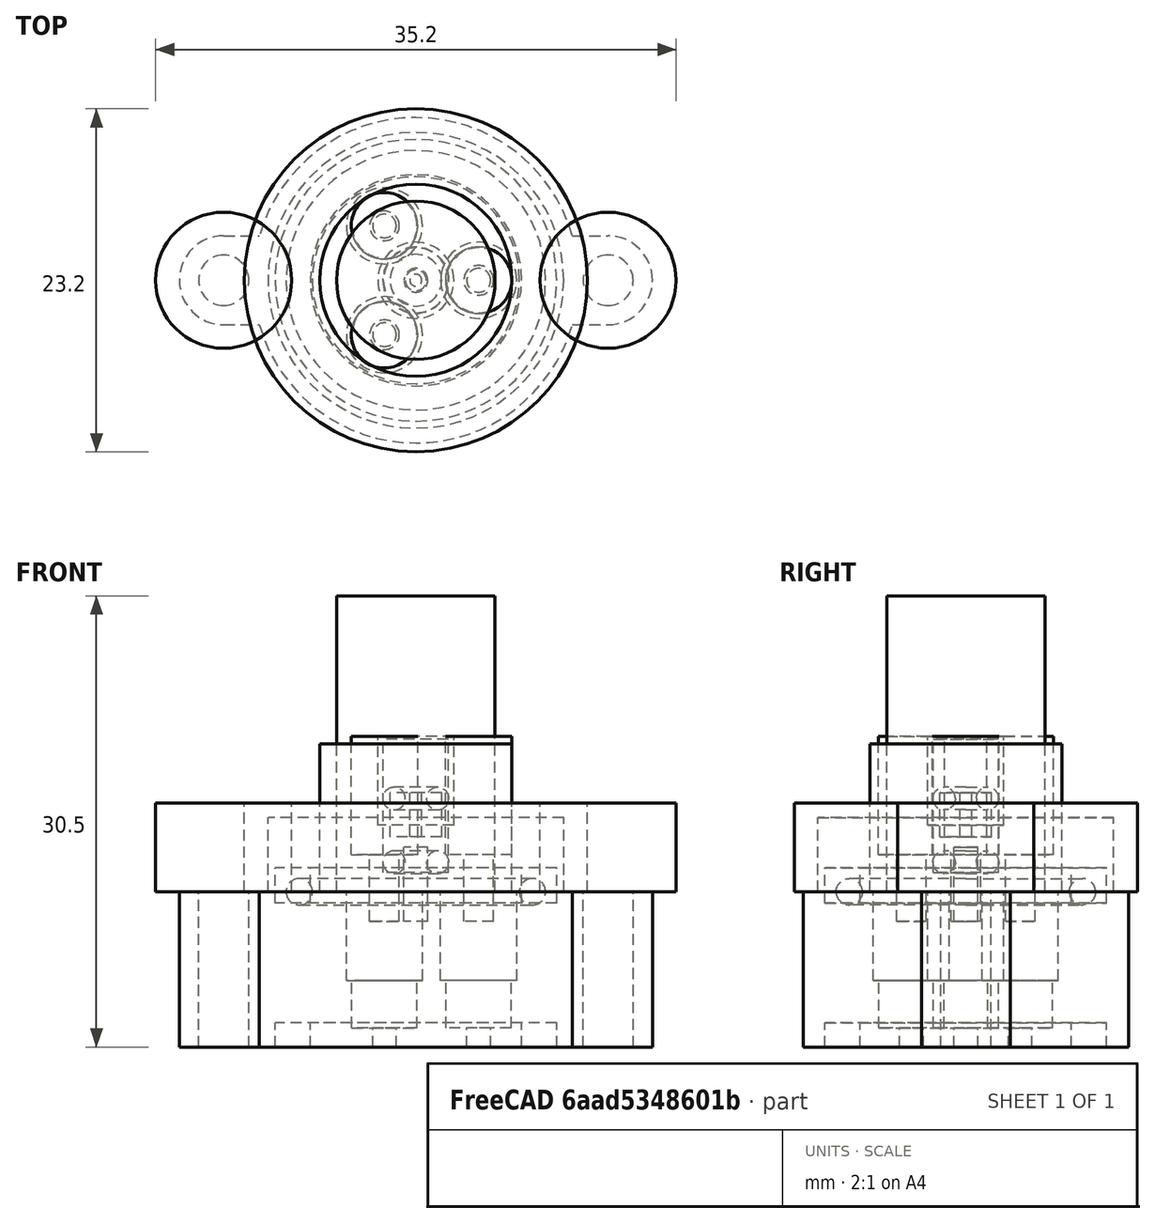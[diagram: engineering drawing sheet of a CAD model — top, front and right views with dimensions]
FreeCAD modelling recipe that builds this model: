
FCSTD DOCUMENT  (FreeCAD 0.17R13509 (Git))
Label: aluminium_ft_insert
License: All rights reserved
LicenseURL: http://en.wikipedia.org/wiki/All_rights_reserved
objects: Part::Cylinder×46, Part::MultiFuse×10, Part::Cut×8, Part::Box×6, Part::FeaturePython×4, Part::Feature×3, App::FeaturePython×1
note: 77 computed .brp shape members not serialized (recipe doc carries the construction recipe); baked Part::Feature solids carry a one-line shape summary decoded from their .brp

FEATURE [Part::Cylinder] Cylinder155  label="Cylinder009"
  Angle = 360
  AttacherType = Attacher::AttachEngine3D
  Height = 2.38125
  Radius = 9.525
  expr: Radius = 3 / 4 * 25.399999999999999 / 2
  expr: Height = 3 / 32 * 25.399999999999999
FEATURE [Part::Cylinder] Cylinder154  label="Cylinder008"
  Angle = 360
  AttacherType = Attacher::AttachEngine3D
  Height = 2.38125
  Radius = 7.14375
  expr: Radius = 9 / 16 * 25.399999999999999 / 2
  expr: Height = 3 / 32 * 25.399999999999999
FEATURE [Part::Feature] Part__Feature001  label="TopOring"
  Placement = pos=(0,0,6.3) rot=(0,0,1;0rad)
  shape: bbox 4.839 x 4.839 x 1.524 mm, 4 faces (baked)
FEATURE [Part::Feature] Part__Feature002  label="BottomOring"
  Placement = pos=(0,0,2) rot=(0,0,1;0rad)
  shape: bbox 4.839 x 4.839 x 1.524 mm, 4 faces (baked)
FEATURE [Part::Cylinder] Cylinder153  label="Body"
  Angle = 360
  AttacherType = Attacher::AttachEngine3D
  Height = 5
  Radius = 10
FEATURE [Part::Cut] Cut019  label="Oring"
  Base = -> Cylinder155
  Placement = pos=(0,0,-0.75) rot=(0,0,1;0rad)
  Tool = -> Cylinder154
FEATURE [Part::Cylinder] Cylinder147  label="ThreadedSection"
  Angle = 360
  AttacherType = Attacher::AttachEngine3D
  Height = 1
  Placement = pos=(0,0,4.5) rot=(0,0,1;0rad)
  Radius = 1
FEATURE [Part::Cylinder] Cylinder149  label="FTBead"
  Angle = 360
  AttacherType = Attacher::AttachEngine3D
  Height = 3
  Placement = pos=(0,0,2.7) rot=(0,0,1;0rad)
  Radius = 1.75
  expr: Radius = 3.5 / 2
FEATURE [Part::Cylinder] Cylinder152  label="RFFeeds005"
  Angle = 360
  AttacherType = Attacher::AttachEngine3D
  Height = 20
  Radius = 5.35813
  expr: Placement.Base.x = 0
FEATURE [Part::Cylinder] Cylinder156  label="BottomWireOutlet"
  Angle = 360
  AttacherType = Attacher::AttachEngine3D
  Height = 5
  Placement = pos=(0,0,-2) rot=(0,0,1;0rad)
  Radius = 1
FEATURE [Part::Cylinder] Cylinder157  label="SealSubtraction"
  Angle = 360
  AttacherType = Attacher::AttachEngine3D
  Height = 8
  Placement = pos=(0,0,2.5) rot=(0,0,1;0rad)
  Radius = 2.25
FEATURE [Part::MultiFuse] Fusion
  Placement = pos=(4.25,0,0) rot=(0,0,1;0rad)
  Shapes = -> [Cylinder147,Cylinder157,Cylinder156]
FEATURE [Part::FeaturePython] Array  label="SealArray"  # Draft array (typed FeaturePython)
  Angle = 360
  ArrayType = 1
  Axis = (0,0,1)
  Base = -> Fusion
  Center = (0,0,0)
  Fuse = false
  IntervalAxis = (0,0,0)
  IntervalX = (1,0,0)
  IntervalY = (0,1,0)
  IntervalZ = (0,0,0)
  NumberPolar = 3
  NumberX = 2
  NumberY = 2
  NumberZ = 1
FEATURE [Part::Cylinder] Cylinder159  label="FTBeadHole"
  Angle = 360
  AttacherType = Attacher::AttachEngine3D
  Height = 17
  Radius = 0.405
  expr: Radius = 0.81000000000000005 / 2
FEATURE [Part::Cut] Cut020
  Base = -> Cylinder149
  Placement = pos=(0,0,1) rot=(0,0,1;0rad)
  Tool = -> Cylinder159
FEATURE [Part::Cylinder] Cylinder160  label="Cylinder010"
  Angle = 360
  AttacherType = Attacher::AttachEngine3D
  Height = 2.38125
  Radius = 9.525
  expr: Radius = 3 / 4 * 25.399999999999999 / 2
  expr: Height = 3 / 32 * 25.399999999999999
FEATURE [Part::Cylinder] Cylinder161  label="WireFeedsMount003"
  Angle = 360
  AttacherType = Attacher::AttachEngine3D
  Height = 11
  Placement = pos=(-13,0,0) rot=(0,0,1;0rad)
  Radius = 1.7
FEATURE [Part::Cylinder] Cylinder162  label="ThreadedSection001"
  Angle = 360
  AttacherType = Attacher::AttachEngine3D
  Height = 6
  Placement = pos=(0,0,4.5) rot=(0,0,1;0rad)
  Radius = 2.575
  expr: Radius = 5.1500000000000004 / 2
FEATURE [Part::Cylinder] Cylinder163  label="Cylinder011"
  Angle = 360
  AttacherType = Attacher::AttachEngine3D
  Height = 2.38125
  Radius = 7.14375
  expr: Radius = 9 / 16 * 25.399999999999999 / 2
  expr: Height = 3 / 32 * 25.399999999999999
FEATURE [Part::Cut] Cut022  label="Oring001"
  Base = -> Cylinder160
  Placement = pos=(0,0,-0.75) rot=(0,0,1;0rad)
  Tool = -> Cylinder163
FEATURE [Part::Cylinder] Cylinder164  label="Body001"
  Angle = 360
  AttacherType = Attacher::AttachEngine3D
  Height = 10.5
  Radius = 11
FEATURE [Part::Cylinder] Cylinder165  label="WireFeedsMount004"
  Angle = 360
  AttacherType = Attacher::AttachEngine3D
  Height = 11
  Placement = pos=(13,0,0) rot=(0,0,1;0rad)
  Radius = 1.7
FEATURE [Part::Cylinder] Cylinder166  label="BottomWireOutlet001"
  Angle = 360
  AttacherType = Attacher::AttachEngine3D
  Height = 5
  Placement = pos=(0,0,-2) rot=(0,0,1;0rad)
  Radius = 0.8
FEATURE [Part::Cylinder] Cylinder167  label="SealSubtraction001"
  Angle = 360
  AttacherType = Attacher::AttachEngine3D
  Height = 9
  Placement = pos=(0,0,1.3) rot=(0,0,1;0rad)
  Radius = 2.2
FEATURE [Part::Box] Box002  label="MountCube003"
  AttacherType = Attacher::AttachEngine3D
  Height = 10.5
  Length = 3
  Placement = pos=(10,-3,0) rot=(0,0,1;0rad)
  Width = 6
FEATURE [Part::Box] Box003  label="MountCube004"
  AttacherType = Attacher::AttachEngine3D
  Height = 10.5
  Length = 3
  Placement = pos=(-13,-3,0) rot=(0,0,1;0rad)
  Width = 6
FEATURE [Part::MultiFuse] Fusion004
  Placement = pos=(4.25,0,0) rot=(0,0,1;0rad)
  Shapes = -> [Cylinder162,Cylinder167,Cylinder166]
FEATURE [Part::Cylinder] Cylinder168  label="MountFlange003"
  Angle = 360
  AttacherType = Attacher::AttachEngine3D
  Height = 10.5
  Placement = pos=(-13,0,0) rot=(0,0,1;0rad)
  Radius = 3
FEATURE [Part::Cylinder] Cylinder169  label="MountFlange004"
  Angle = 360
  AttacherType = Attacher::AttachEngine3D
  Height = 10.5
  Placement = pos=(13,0,0) rot=(0,0,1;0rad)
  Radius = 3
FEATURE [Part::MultiFuse] Fusion003
  Shapes = -> [Cylinder169,Box002,Box003,Cylinder168,Cylinder164]
FEATURE [Part::FeaturePython] Array001  label="SealArray001"  # Draft array (typed FeaturePython)
  Angle = 360
  ArrayType = 1
  Axis = (0,0,1)
  Base = -> Fusion004
  Center = (0,0,0)
  Fuse = false
  IntervalAxis = (0,0,0)
  IntervalX = (1,0,0)
  IntervalY = (0,1,0)
  IntervalZ = (0,0,0)
  NumberPolar = 3
  NumberX = 2
  NumberY = 2
  NumberZ = 1
FEATURE [Part::MultiFuse] Fusion005
  Shapes = -> [Cylinder165,Cylinder161,Cut022,Array001]
FEATURE [Part::Cut] Cut021
  Base = -> Fusion003
  Placement = pos=(0,0,-10.5) rot=(0,0,1;0rad)
  Tool = -> Fusion005
FEATURE [Part::Cylinder] Cylinder170  label="Cylinder012"
  Angle = 360
  AttacherType = Attacher::AttachEngine3D
  Height = 2.38125
  Radius = 9.525
  expr: Radius = 3 / 4 * 25.399999999999999 / 2
  expr: Height = 3 / 32 * 25.399999999999999
FEATURE [Part::Cylinder] Cylinder171  label="WireFeedsMount005"
  Angle = 360
  AttacherType = Attacher::AttachEngine3D
  Height = 11
  Placement = pos=(-13,0,0) rot=(0,0,1;0rad)
  Radius = 1.7
FEATURE [Part::Cylinder] Cylinder172  label="ThreadedSection002"
  Angle = 360
  AttacherType = Attacher::AttachEngine3D
  Height = 6
  Placement = pos=(0,0,4.5) rot=(0,0,1;0rad)
  Radius = 2.575
  expr: Radius = 5.1500000000000004 / 2
FEATURE [Part::Cylinder] Cylinder173  label="Cylinder013"
  Angle = 360
  AttacherType = Attacher::AttachEngine3D
  Height = 2.38125
  Radius = 7.14375
  expr: Radius = 9 / 16 * 25.399999999999999 / 2
  expr: Height = 3 / 32 * 25.399999999999999
FEATURE [Part::Cut] Cut024  label="Oring002"
  Base = -> Cylinder170
  Placement = pos=(0,0,-0.75) rot=(0,0,1;0rad)
  Tool = -> Cylinder173
FEATURE [Part::Cylinder] Cylinder174  label="Body002"
  Angle = 360
  AttacherType = Attacher::AttachEngine3D
  Height = 10.5
  Radius = 11
FEATURE [Part::Cylinder] Cylinder175  label="WireFeedsMount006"
  Angle = 360
  AttacherType = Attacher::AttachEngine3D
  Height = 11
  Placement = pos=(13,0,0) rot=(0,0,1;0rad)
  Radius = 1.7
FEATURE [Part::Cylinder] Cylinder176  label="BottomWireOutlet002"
  Angle = 360
  AttacherType = Attacher::AttachEngine3D
  Height = 5
  Placement = pos=(0,0,-2) rot=(0,0,1;0rad)
  Radius = 0.8
FEATURE [Part::Cylinder] Cylinder177  label="SealSubtraction002"
  Angle = 360
  AttacherType = Attacher::AttachEngine3D
  Height = 9
  Placement = pos=(0,0,1.3) rot=(0,0,1;0rad)
  Radius = 2.2
FEATURE [Part::Box] Box004  label="MountCube005"
  AttacherType = Attacher::AttachEngine3D
  Height = 10.5
  Length = 3
  Placement = pos=(10,-3,0) rot=(0,0,1;0rad)
  Width = 6
FEATURE [App::FeaturePython] SetupSheet002  # Path/CAM operation (typed FeaturePython)
  ClearanceHeightExpression = StartDepth+SetupSheet.ClearanceHeightOffset
  ClearanceHeightOffset = 5
  FinalDepthExpression = OpFinalDepth
  HorizRapid = 0
  SafeHeightExpression = StartDepth+SetupSheet.SafeHeightOffset
  SafeHeightOffset = 3
  StartDepthExpression = OpStartDepth
  StepDownExpression = OpToolDiameter
  VertRapid = 0
FEATURE [Part::Box] Box005  label="MountCube006"
  AttacherType = Attacher::AttachEngine3D
  Height = 10.5
  Length = 3
  Placement = pos=(-13,-3,0) rot=(0,0,1;0rad)
  Width = 6
FEATURE [Part::MultiFuse] Fusion007
  Placement = pos=(4.25,0,0) rot=(0,0,1;0rad)
  Shapes = -> [Cylinder172,Cylinder177,Cylinder176]
FEATURE [Part::Cylinder] Cylinder178  label="MountFlange005"
  Angle = 360
  AttacherType = Attacher::AttachEngine3D
  Height = 10.5
  Placement = pos=(-13,0,0) rot=(0,0,1;0rad)
  Radius = 3
FEATURE [Part::Cylinder] Cylinder179  label="MountFlange006"
  Angle = 360
  AttacherType = Attacher::AttachEngine3D
  Height = 10.5
  Placement = pos=(13,0,0) rot=(0,0,1;0rad)
  Radius = 3
FEATURE [Part::MultiFuse] Fusion006
  Shapes = -> [Cylinder179,Box004,Box005,Cylinder178,Cylinder174]
FEATURE [Part::FeaturePython] Array002  label="SealArray002"  # Draft array (typed FeaturePython)
  Angle = 360
  ArrayType = 1
  Axis = (0,0,1)
  Base = -> Fusion007
  Center = (0,0,0)
  Fuse = false
  IntervalAxis = (0,0,0)
  IntervalX = (1,0,0)
  IntervalY = (0,1,0)
  IntervalZ = (0,0,0)
  NumberPolar = 3
  NumberX = 2
  NumberY = 2
  NumberZ = 1
FEATURE [Part::MultiFuse] Fusion008
  Shapes = -> [Cylinder175,Cylinder171,Cut024,Array002]
FEATURE [Part::Cut] Cut023
  Base = -> Fusion006
  Placement = pos=(0,0,-10.5) rot=(0,0,1;0rad)
  Tool = -> Fusion008
FEATURE [Part::Cylinder] Cylinder180  label="Cylinder014"
  Angle = 360
  AttacherType = Attacher::AttachEngine3D
  Height = 2.38125
  Radius = 7.14375
  expr: Radius = 9 / 16 * 25.399999999999999 / 2
  expr: Height = 3 / 32 * 25.399999999999999
FEATURE [Part::Cylinder] Cylinder181  label="MountFlange007"
  Angle = 360
  AttacherType = Attacher::AttachEngine3D
  Height = 10.5
  Placement = pos=(-13,0,0) rot=(0,0,1;0rad)
  Radius = 3
FEATURE [Part::Box] Box006  label="MountCube007"
  AttacherType = Attacher::AttachEngine3D
  Height = 10.5
  Length = 3
  Placement = pos=(-13,-3,0) rot=(0,0,1;0rad)
  Width = 6
FEATURE [Part::Cylinder] Cylinder182  label="WireFeedsMount007"
  Angle = 360
  AttacherType = Attacher::AttachEngine3D
  Height = 11
  Placement = pos=(13,0,0) rot=(0,0,1;0rad)
  Radius = 1.7
FEATURE [Part::Box] Box007  label="MountCube008"
  AttacherType = Attacher::AttachEngine3D
  Height = 10.5
  Length = 3
  Placement = pos=(10,-3,0) rot=(0,0,1;0rad)
  Width = 6
FEATURE [Part::Cylinder] Cylinder183  label="WireFeedsMount008"
  Angle = 360
  AttacherType = Attacher::AttachEngine3D
  Height = 11
  Placement = pos=(-13,0,0) rot=(0,0,1;0rad)
  Radius = 1.7
FEATURE [Part::Cylinder] Cylinder184  label="Body003"
  Angle = 360
  AttacherType = Attacher::AttachEngine3D
  Height = 10.5
  Radius = 11
FEATURE [Part::Cylinder] Cylinder185  label="MountFlange008"
  Angle = 360
  AttacherType = Attacher::AttachEngine3D
  Height = 10.5
  Placement = pos=(13,0,0) rot=(0,0,1;0rad)
  Radius = 3
FEATURE [Part::Cylinder] Cylinder186  label="BottomWireOutlet003"
  Angle = 360
  AttacherType = Attacher::AttachEngine3D
  Height = 5
  Placement = pos=(0,0,-2) rot=(0,0,1;0rad)
  Radius = 0.8
FEATURE [Part::MultiFuse] Fusion011
  Shapes = -> [Cylinder185,Box007,Box006,Cylinder181,Cylinder184]
FEATURE [Part::Cylinder] Cylinder187  label="ThreadedSection003"
  Angle = 360
  AttacherType = Attacher::AttachEngine3D
  Height = 6
  Placement = pos=(0,0,4.5) rot=(0,0,1;0rad)
  Radius = 2.575
  expr: Radius = 5.1500000000000004 / 2
FEATURE [Part::Cylinder] Cylinder188  label="Cylinder015"
  Angle = 360
  AttacherType = Attacher::AttachEngine3D
  Height = 2.38125
  Radius = 9.525
  expr: Radius = 3 / 4 * 25.399999999999999 / 2
  expr: Height = 3 / 32 * 25.399999999999999
FEATURE [Part::Cut] Cut025  label="Oring003"
  Base = -> Cylinder188
  Placement = pos=(0,0,-0.75) rot=(0,0,1;0rad)
  Tool = -> Cylinder180
FEATURE [Part::Cylinder] Cylinder189  label="SealSubtraction003"
  Angle = 360
  AttacherType = Attacher::AttachEngine3D
  Height = 9
  Placement = pos=(0,0,1.3) rot=(0,0,1;0rad)
  Radius = 2.2
FEATURE [Part::MultiFuse] Fusion009
  Placement = pos=(4.25,0,0) rot=(0,0,1;0rad)
  Shapes = -> [Cylinder187,Cylinder189,Cylinder186]
FEATURE [Part::FeaturePython] Array003  label="SealArray003"  # Draft array (typed FeaturePython)
  Angle = 360
  ArrayType = 1
  Axis = (0,0,1)
  Base = -> Fusion009
  Center = (0,0,0)
  Fuse = false
  IntervalAxis = (0,0,0)
  IntervalX = (1,0,0)
  IntervalY = (0,1,0)
  IntervalZ = (0,0,0)
  NumberPolar = 3
  NumberX = 2
  NumberY = 2
  NumberZ = 1
FEATURE [Part::MultiFuse] Fusion010
  Shapes = -> [Cylinder182,Cylinder183,Cut025,Array003]
FEATURE [Part::Cut] Cut026
  Base = -> Fusion011
  Placement = pos=(0,0,-10.5) rot=(0,0,1;0rad)
  Tool = -> Fusion010
FEATURE [Part::Cylinder] Cylinder192  label="ThreadedSection004"
  Angle = 360
  AttacherType = Attacher::AttachEngine3D
  Height = 6
  Placement = pos=(0,0,4.5) rot=(0,0,1;0rad)
  Radius = 2.575
  expr: Radius = 5.1500000000000004 / 2
FEATURE [Part::Cylinder] Cylinder196  label="BottomWireOutlet004"
  Angle = 360
  AttacherType = Attacher::AttachEngine3D
  Height = 5
  Placement = pos=(0,0,-2) rot=(0,0,1;0rad)
  Radius = 0.8
FEATURE [Part::Cylinder] Cylinder197  label="SealSubtraction004"
  Angle = 360
  AttacherType = Attacher::AttachEngine3D
  Height = 9
  Placement = pos=(0,0,1.3) rot=(0,0,1;0rad)
  Radius = 2.2
FEATURE [Part::Cylinder] Cylinder198  label="Cylinder"
  Angle = 360
  AttacherType = Attacher::AttachEngine3D
  Height = 6
  Radius = 11.6
FEATURE [Part::Cylinder] Cylinder199  label="Cylinder016"
  Angle = 360
  AttacherType = Attacher::AttachEngine3D
  Height = 6
  Placement = pos=(-13,0,0) rot=(0,0,1;0rad)
  Radius = 4.6
FEATURE [Part::Cylinder] Cylinder200  label="Cylinder017"
  Angle = 360
  AttacherType = Attacher::AttachEngine3D
  Height = 6
  Placement = pos=(13,0,0) rot=(0,0,1;0rad)
  Radius = 4.6
FEATURE [Part::Feature] Part__Feature  label="9464K21"
  shape: bbox 19 x 19 x 1.778 mm, 4 faces (baked)
FEATURE [Part::Cylinder] Cylinder  label="Cylinder018"
  Angle = 360
  AttacherType = Attacher::AttachEngine3D
  Height = 10
  Radius = 6.5
